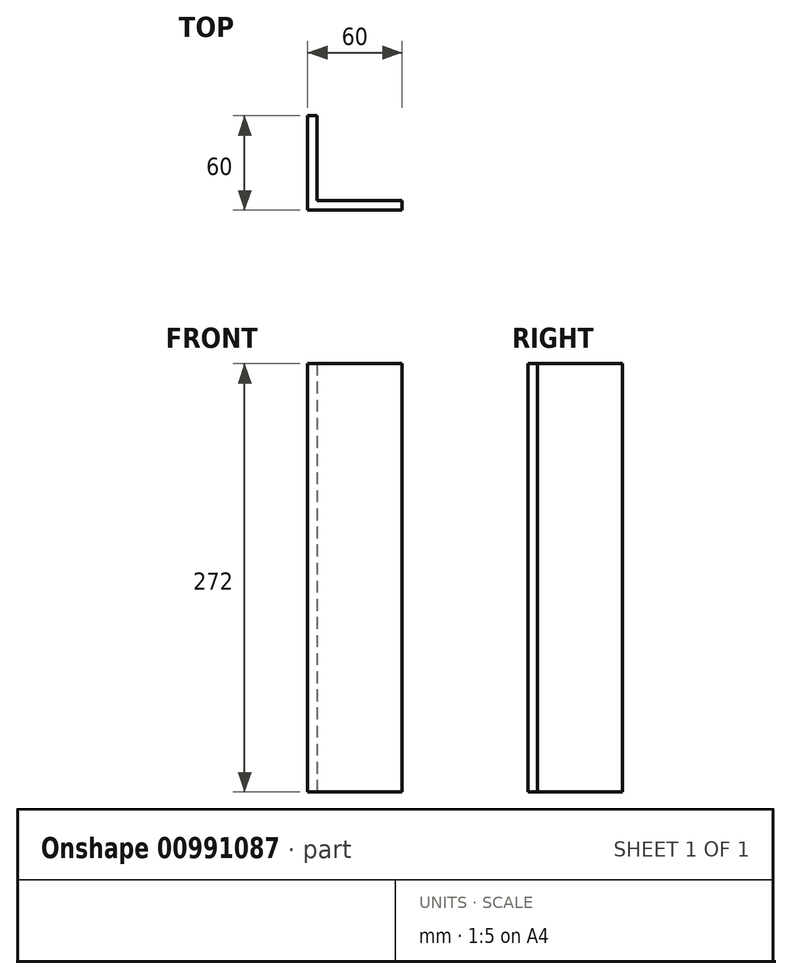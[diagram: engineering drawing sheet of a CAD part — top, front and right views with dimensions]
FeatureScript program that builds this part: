
annotation { "Feature Type Name" : "Feature", "Feature Type Description" : "" }
export const myFeature = defineFeature(function(context is Context, id is Id, definition is map)
    precondition{}
    {
        {
            var Q0;
            Q0=qCreatedBy(makeId("Top.planeOp"),FACE);
            var sketch = newSketch(context, id + "F0", { "sketchPlane" : qUnion([Q0])});
            skLineSegment(sketch, "E0", {"start": v(0, 0) * mm, "end": v(0, 60) * mm});
            skLineSegment(sketch, "E1", {"start": v(0, 0) * mm, "end": v(60, 0) * mm});
            skLineSegment(sketch, "E2.0", {"start": v(6, 6) * mm, "end": v(6, 60) * mm});
            skLineSegment(sketch, "E2.1", {"start": v(6, 6) * mm, "end": v(60, 6) * mm});
            skLineSegment(sketch, "E3", {"start": v(6, 60) * mm, "end": v(0, 60) * mm});
            skLineSegment(sketch, "E4", {"start": v(60, 0) * mm, "end": v(60, 6) * mm});
            skSolve(sketch);
        }
        {
            var Q0;
            Q0=makeQuery(id+"F0.imprint","IMPRINT",FACE,{"disambiguationData":[TD([[makeQuery(id+"F0.imprint","IMPRINT",EDGE,{"derivedFrom":sQuery(id+"F0.wireOp",EDGE,"E0")}),-1.0]])]});
            extrude(context, id + "F1", {"entities" : qUnion([Q0]), "depth" : 272 * mm, "offsetDistance" : 25 * mm});
        }
    });
